# Revit family: GR_Решетка_РАГ(Р)_Вытяжка_LOD300_R21
name_source: partatom
category: Воздухораспределители
units: mm (PartAtom-declared; Revit-internal decimal feet)

## family parameters
Всегда вертикально = Да
Заголовок OmniClass = Diffusers, Registers, and Grilles
На основе рабочей плоскости = Нет
Номер OmniClass = 23.75.70.21.27.11
Общий = Нет
При загрузке вырезать с полостями = Да
Размер круглого соединителя = Использовать диаметр
Тип детали = Нормальный
Точка принадлежности помещению = Нет

## types (6) — shared parameters
ADSK_URL страницы изделия = https://grilles.ru
ADSK_Автор = THE GRILLES
ADSK_Версия Revit = 2021
ADSK_Версия семейства = v1
ADSK_Единица измерения = шт.
ADSK_Завод-изготовитель = ООО "ВЕНТРЕШЕТКИКОМ"
ADSK_Количество = 1
GR_Материал КРВ = ADSK_Оцинкованная сталь
GR_Материал решетки = Сталь, RAL 9016M, белый
URL = https://grilles.ru
Изготовитель = ООО "ВЕНТРЕШЕТКИКОМ"
О = ♠ : 0°
О15 = ♠ : 15°
О30 = ♠ : 30°
О45 = ♠ : 45°
О60 = ♠ : 60°
О75 = ♠ : 75°
О90 = ♠ : 90°
zero-valued in all types: Отметка по умолчанию

## per-type parameters (varying)
| type | ADSK_Код изделия | ADSK_Наименование | КЖС | КРВ | Марка_Тип | Масса_Тип | Описание |
| РАГ | 002029 | Решетка регулируемая вытяжная РАГ | 0.79 | Нет | РАГ_Mark | РАГ_M | Регулируемая решетка РАГ используются в приточно-вытяжной вентиляции и системах кондиционирования воздуха и предназначены для регулировки направления воздушного потока вверх и вниз. Монтируются в вентиляционные каналы и строительные проемы различных типов. |
| РАГ-Р | 000160 | Решетка регулируемая вытяжная с клапаном РАГ-Р | 0.79 | Да | РАГ_Mark | РАГ_M | Регулируемая решетка РАГ-Р с клапаном расхода воздуха КРВ) используются в приточно-вытяжной вентиляции и системах кондиционирования воздуха. Решетка предназначена для регулировки направления воздушного потока вверх и вниз а КРВ регулирует объем подаваемого воздуха. Монтируются решетки в вентиляционные каналы и строительные проемы различных типов. |
| РАГ-В | 002034 | Решетка регулируемая вертикальная вытяжная РАГ-В | 0.79 | Нет | РАГ-В_Мark | РАГ-В_М | Регулируемая решетка с вертикальными жалюзи РАГ-В используются в приточно-вытяжной вентиляции и системах кондиционирования воздуха. Решетка предназначена для регулировки направления воздушного потока вправо и влево. Монтируются решетки в вентиляционные каналы и строительные проемы различных типов. |
| РАГ-В-Р | 000161 | Решетка регулируемая вертикальная вытяжная с клапаном РАГ-В-Р | 0.79 | Да | РАГ-В_Мark | РАГ-В_М | Регулируемая решетка РАГ-В+Р с клапаном расхода воздуха КРВ) используются в приточно-вытяжной вентиляции и системах кондиционирования воздуха. Решетка предназначена для регулировки направления воздушного потока вверх и вниз а КРВ регулирует объем подаваемого воздуха. Монтируются решетки в вентиляционные каналы и строительные проемы различных типов. |
| РАГ-М | 002037 | Решетка с регулируемыми жалюзи вытяжная РАГ-М | 0.78 | Нет | РАГ-М_Мark | РАГ-М_М | Регулируемые решетки РАГ-М используются в системах вентиляции и кондиционирования для подачи свежего воздуха и удаления вытяжного воздуха из помещений. Они могут быть установлены в отводы воздуховодов адаптеры из оцинкованной стали или любые другие потолочные и стеновые проёмы для декорирования элементов систем вентиляции в помещениях любого назначения – производственных цехах административных жилых и офисных помещениях. |
| РАГ-М-Р | 000164 | Решетка с регулируемыми жалюзи вытяжная с клапаном РАГ-М-Р | 0.78 | Да | РАГ-М_Мark | РАГ-М_М | Регулируемые решетки РАГ-М+Р с клапаном расхода воздуха (КРВ) используются в системах вентиляции и кондиционирования для подачи свежего воздуха и удаления вытяжного воздуха из помещений. Они могут быть установлены в отводы воздуховодов адаптеры из оцинкованной стали или любые другие потолочные и стеновые проёмы для декорирования элементов систем вентиляции или воздушного отопления. |
